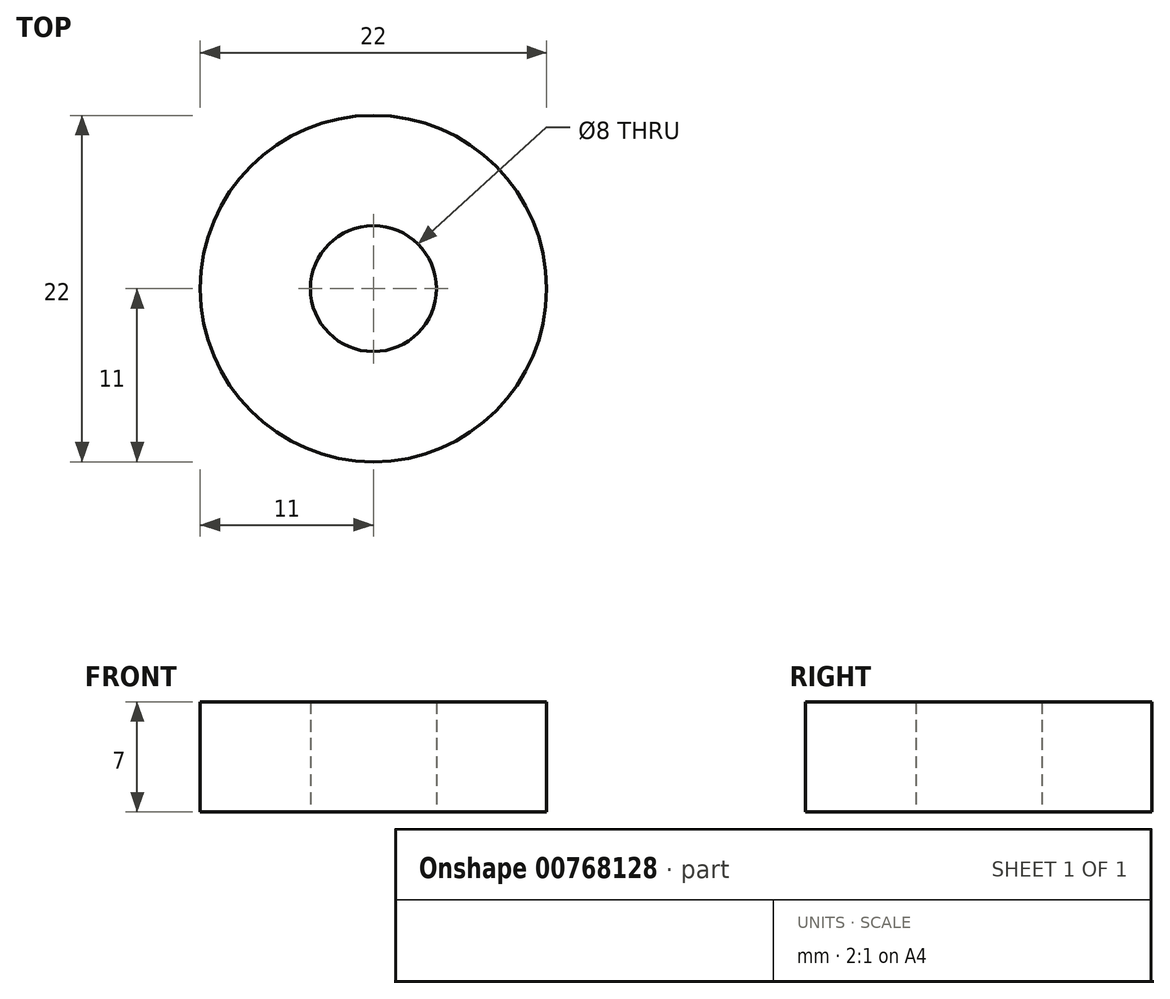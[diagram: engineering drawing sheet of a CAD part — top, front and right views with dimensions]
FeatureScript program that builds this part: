
annotation { "Feature Type Name" : "Feature", "Feature Type Description" : "" }
export const myFeature = defineFeature(function(context is Context, id is Id, definition is map)
    precondition{}
    {
        {
            var Q0;
            Q0=qCreatedBy(makeId("Top.planeOp"),FACE);
            var sketch = newSketch(context, id + "F0", { "sketchPlane" : qUnion([Q0])});
            skCircle(sketch, "E0", {"center": v(0, 0) * mm, "radius": 11 * mm});
            skCircle(sketch, "E1", {"center": v(0, 0) * mm, "radius": 4 * mm});
            skSolve(sketch);
        }
        {
            var Q0;
            Q0=makeQuery(id+"F0.imprint","IMPRINT",FACE,{"disambiguationData":[TD([[makeQuery(id+"F0.imprint","IMPRINT",EDGE,{"derivedFrom":sQuery(id+"F0.wireOp",EDGE,"E0")}),1.0]])]});
            extrude(context, id + "F1", {"entities" : qUnion([Q0]), "endBound" : BoundingType.SYMMETRIC, "depth" : 7 * mm, "offsetDistance" : 25 * mm});
        }
    });
